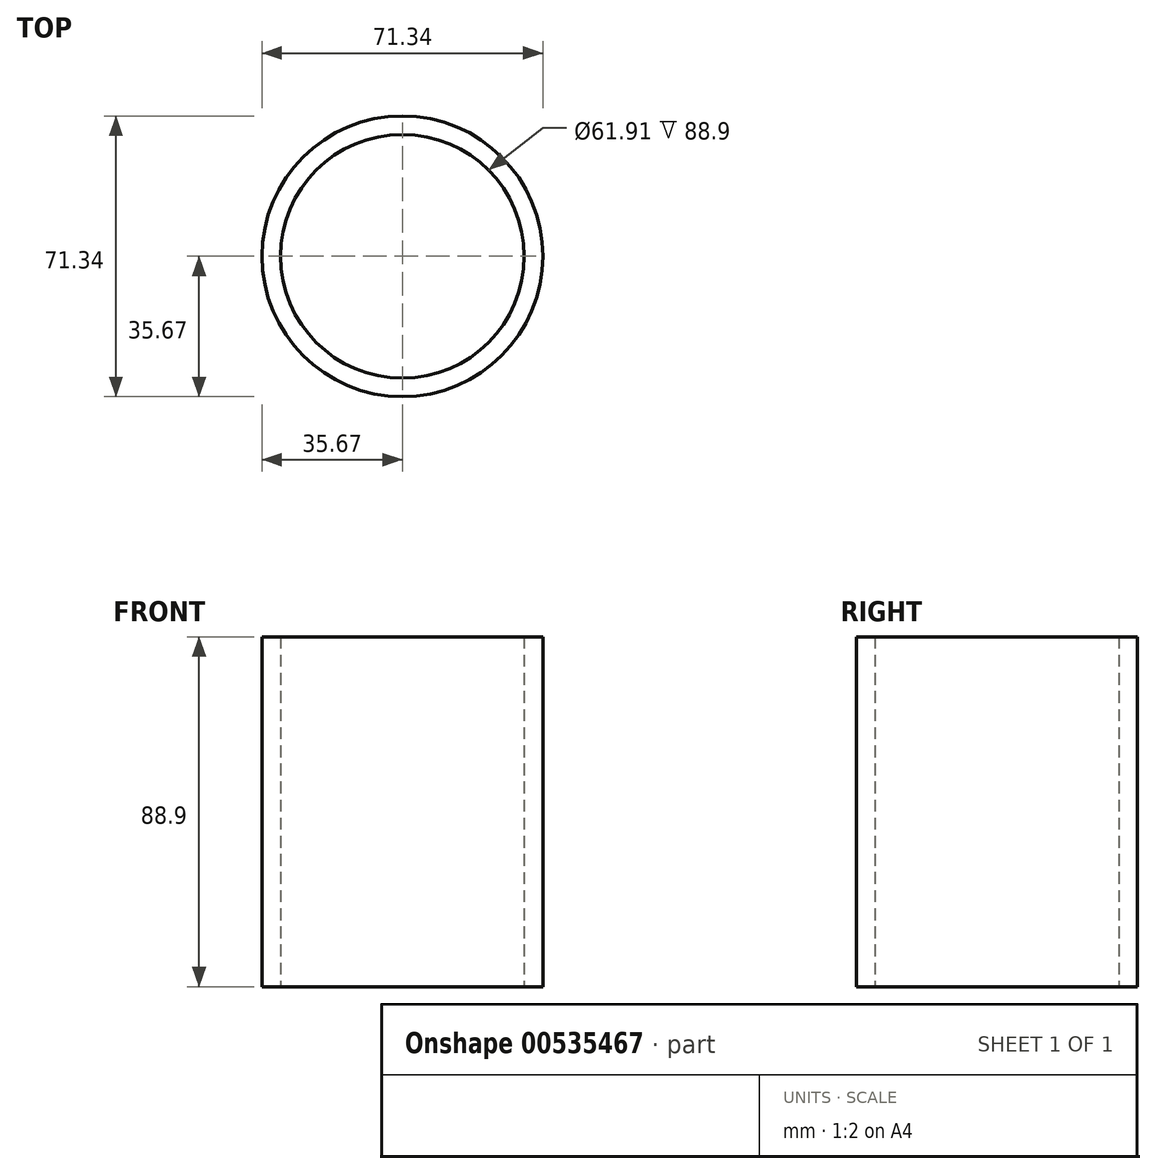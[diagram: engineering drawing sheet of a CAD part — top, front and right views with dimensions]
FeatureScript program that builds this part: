
annotation { "Feature Type Name" : "Feature", "Feature Type Description" : "" }
export const myFeature = defineFeature(function(context is Context, id is Id, definition is map)
    precondition{}
    {
        {
            var Q0;
            Q0=qCreatedBy(makeId("Top.planeOp"),FACE);
            var sketch = newSketch(context, id + "F0", { "sketchPlane" : qUnion([Q0])});
            skCircle(sketch, "E0", {"center": v(0, 0) * mm, "radius": 30.96 * mm});
            skCircle(sketch, "E1", {"center": v(0, 0) * mm, "radius": 35.67 * mm});
            skSolve(sketch);
        }
        {
            var Q0;
            Q0=makeQuery(id+"F0.imprint","IMPRINT",FACE,{"disambiguationData":[TD([[makeQuery(id+"F0.imprint","IMPRINT",EDGE,{"derivedFrom":sQuery(id+"F0.wireOp",EDGE,"E0")}),-1.0]])]});
            extrude(context, id + "F1", {"entities" : qUnion([Q0]), "depth" : 88.9 * mm, "offsetDistance" : 25.4 * mm});
        }
    });
